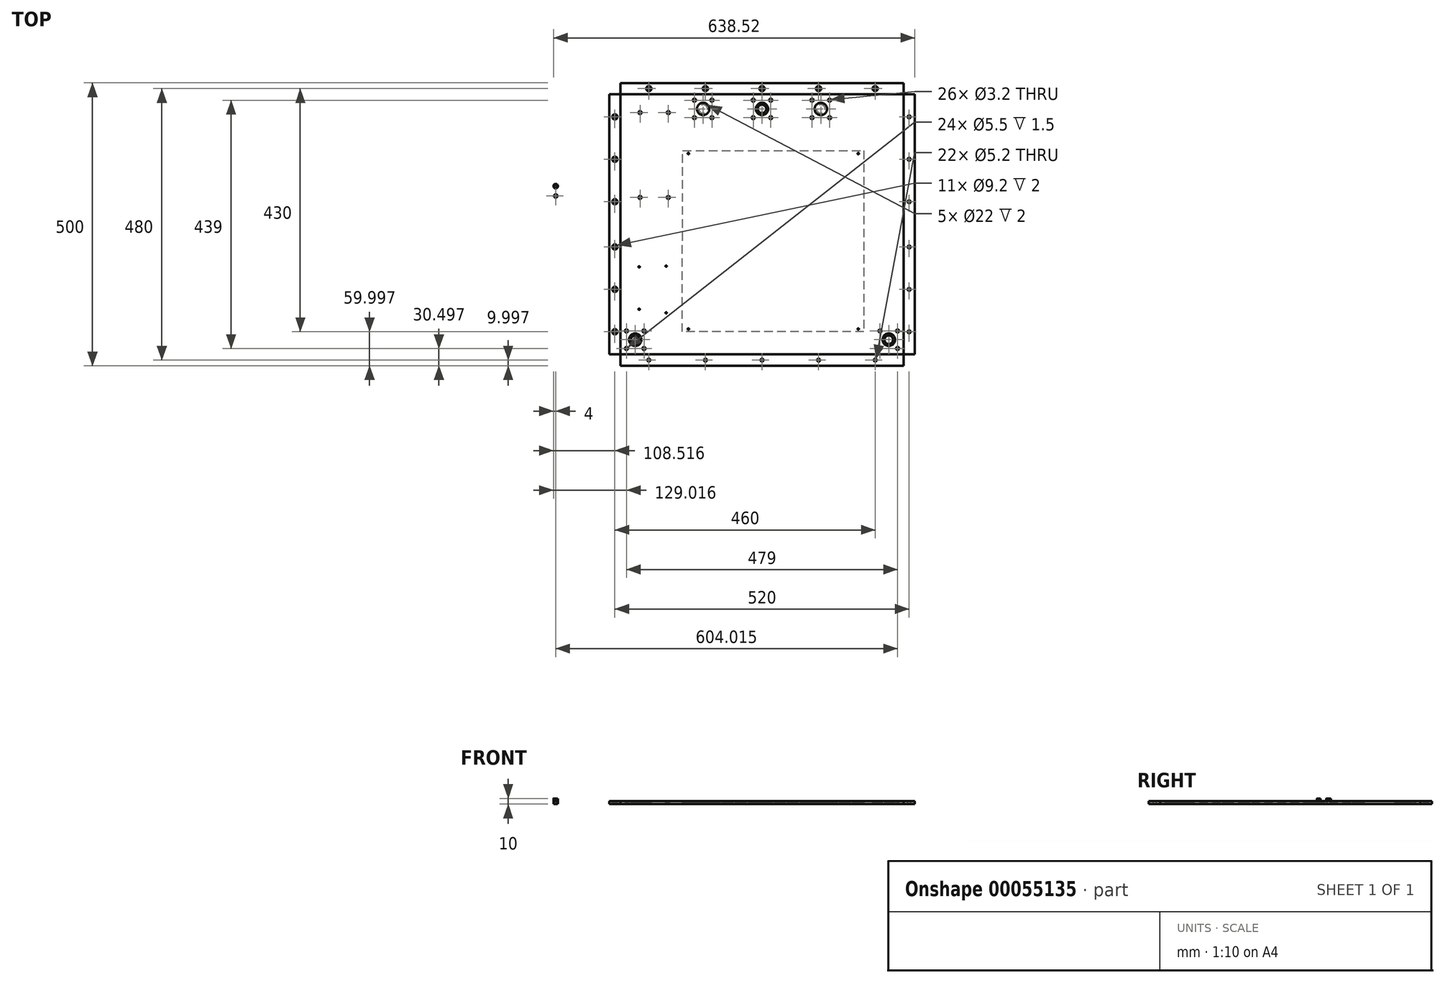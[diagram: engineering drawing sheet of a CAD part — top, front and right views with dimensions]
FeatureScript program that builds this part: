
annotation { "Feature Type Name" : "Feature", "Feature Type Description" : "" }
export const myFeature = defineFeature(function(context is Context, id is Id, definition is map)
    precondition{}
    {
        {
            var Q0;
            Q0=qCreatedBy(makeId("Top.planeOp"),FACE);
            var sketch = newSketch(context, id + "F0", { "sketchPlane" : qUnion([Q0])});
            skLineSegment(sketch, "E0.bottom", {"start": v(-237.36, 309.29) * mm, "end": v(262.64, 309.29) * mm, "construction": true});
            skLineSegment(sketch, "E0.top", {"start": v(-237.36, -150.71) * mm, "end": v(262.64, -150.71) * mm, "construction": true});
            skLineSegment(sketch, "E0.left", {"start": v(-237.36, 309.29) * mm, "end": v(-237.36, -150.71) * mm, "construction": true});
            skLineSegment(sketch, "E0.right", {"start": v(262.64, 309.29) * mm, "end": v(262.64, -150.71) * mm, "construction": true});
            skLineSegment(sketch, "E1.0", {"start": v(-118.36, 309.29) * mm, "end": v(-118.36, -150.71) * mm, "construction": true});
            skLineSegment(sketch, "E2.0", {"start": v(-237.36, 94.29) * mm, "end": v(-117.36, 94.29) * mm, "construction": true});
            skLineSegment(sketch, "E3.0", {"start": v(-202.86, 309.29) * mm, "end": v(-202.86, 94.29) * mm, "construction": true});
            skLineSegment(sketch, "E4.0", {"start": v(-152.86, 309.29) * mm, "end": v(-152.86, 94.29) * mm, "construction": true});
            skLineSegment(sketch, "E5.0", {"start": v(-201.3, 276.79) * mm, "end": v(-118.36, 276.79) * mm, "construction": true});
            skLineSegment(sketch, "E6.0", {"start": v(-201.3, 126.79) * mm, "end": v(-118.36, 126.79) * mm, "construction": true});
            skCircle(sketch, "E7", {"center": v(-202.86, 276.79) * mm, "radius": 1.6 * mm});
            skCircle(sketch, "E8", {"center": v(-152.86, 276.79) * mm, "radius": 1.6 * mm});
            skCircle(sketch, "E9", {"center": v(-152.86, 126.79) * mm, "radius": 1.6 * mm});
            skCircle(sketch, "E10", {"center": v(-202.86, 126.79) * mm, "radius": 1.6 * mm});
            skLineSegment(sketch, "E11.0", {"start": v(182.64, 309.29) * mm, "end": v(182.64, -150.71) * mm, "construction": true});
            skLineSegment(sketch, "E12.0", {"start": v(-117.36, 309.29) * mm, "end": v(-117.36, -150.71) * mm, "construction": true});
            skLineSegment(sketch, "E13.0", {"start": v(197.64, 309.29) * mm, "end": v(197.64, -150.71) * mm, "construction": true});
            skLineSegment(sketch, "E14.0", {"start": v(-132.36, 309.29) * mm, "end": v(-132.36, -150.71) * mm, "construction": true});
            skLineSegment(sketch, "E15.0", {"start": v(-237.36, -140.21) * mm, "end": v(262.64, -140.21) * mm, "construction": true});
            skLineSegment(sketch, "E16.0", {"start": v(-237.36, 298.79) * mm, "end": v(262.64, 298.79) * mm, "construction": true});
            skLineSegment(sketch, "E17.0", {"start": v(-237.36, -109.21) * mm, "end": v(262.64, -109.21) * mm, "construction": true});
            skLineSegment(sketch, "E18.trimOffspring", {"start": v(-226.86, -109.21) * mm, "end": v(-226.86, -140.21) * mm, "construction": true});
            skLineSegment(sketch, "E19.trimOffspring", {"start": v(-195.86, -109.21) * mm, "end": v(-195.86, -140.21) * mm, "construction": true});
            skLineSegment(sketch, "E20", {"start": v(-226.86, -124.71) * mm, "end": v(-195.86, -124.71) * mm, "construction": true});
            skCircle(sketch, "E21", {"center": v(-226.86, -109.21) * mm, "radius": 1.6 * mm});
            skCircle(sketch, "E22", {"center": v(-195.86, -109.21) * mm, "radius": 1.6 * mm});
            skCircle(sketch, "E23", {"center": v(-195.86, -140.21) * mm, "radius": 1.6 * mm});
            skCircle(sketch, "E24", {"center": v(-226.86, -140.21) * mm, "radius": 1.6 * mm});
            skLineSegment(sketch, "E25.trimOffspring", {"start": v(252.14, -109.21) * mm, "end": v(252.14, -140.21) * mm, "construction": true});
            skLineSegment(sketch, "E26.trimOffspring", {"start": v(221.14, -109.21) * mm, "end": v(221.14, -140.21) * mm, "construction": true});
            skLineSegment(sketch, "E27", {"start": v(221.14, -124.71) * mm, "end": v(252.14, -124.71) * mm, "construction": true});
            skCircle(sketch, "E28", {"center": v(221.14, -109.21) * mm, "radius": 1.6 * mm});
            skCircle(sketch, "E29", {"center": v(252.14, -109.21) * mm, "radius": 1.6 * mm});
            skCircle(sketch, "E30", {"center": v(221.14, -140.21) * mm, "radius": 1.6 * mm});
            skCircle(sketch, "E31", {"center": v(252.14, -140.21) * mm, "radius": 1.6 * mm});
            skLineSegment(sketch, "E32.0", {"start": v(-106.86, 309.29) * mm, "end": v(-106.86, 199.29) * mm, "construction": true});
            skLineSegment(sketch, "E33.trimOffspring", {"start": v(197.64, -100.71) * mm, "end": v(262.64, -100.71) * mm, "construction": true});
            skLineSegment(sketch, "E34.trimOffspring", {"start": v(-118.36, 199.29) * mm, "end": v(182.64, 199.29) * mm, "construction": true});
            skLineSegment(sketch, "E35.trimOffspring", {"start": v(-118.36, -100.71) * mm, "end": v(182.64, -100.71) * mm, "construction": true});
            skLineSegment(sketch, "E36.0", {"start": v(132.14, 199.29) * mm, "end": v(132.14, 309.29) * mm, "construction": true});
            skLineSegment(sketch, "E37.0", {"start": v(-75.86, 298.79) * mm, "end": v(-75.86, 267.79) * mm, "construction": true});
            skLineSegment(sketch, "E38.0", {"start": v(101.14, 267.79) * mm, "end": v(101.14, 298.79) * mm, "construction": true});
            skLineSegment(sketch, "E39.0", {"start": v(-237.36, 267.79) * mm, "end": v(262.64, 267.79) * mm, "construction": true});
            skLineSegment(sketch, "E40", {"start": v(101.14, 283.29) * mm, "end": v(132.14, 283.29) * mm, "construction": true});
            skLineSegment(sketch, "E41", {"start": v(-75.86, 283.29) * mm, "end": v(-106.86, 283.29) * mm, "construction": true});
            skCircle(sketch, "E42", {"center": v(101.14, 298.79) * mm, "radius": 1.6 * mm});
            skCircle(sketch, "E43", {"center": v(101.14, 267.79) * mm, "radius": 1.6 * mm});
            skCircle(sketch, "E44", {"center": v(132.14, 298.79) * mm, "radius": 1.6 * mm});
            skCircle(sketch, "E45", {"center": v(132.14, 267.79) * mm, "radius": 1.6 * mm});
            skCircle(sketch, "E46", {"center": v(-75.86, 267.79) * mm, "radius": 1.6 * mm});
            skCircle(sketch, "E47", {"center": v(-75.86, 298.79) * mm, "radius": 1.6 * mm});
            skCircle(sketch, "E48", {"center": v(-106.86, 298.79) * mm, "radius": 1.6 * mm});
            skCircle(sketch, "E49", {"center": v(-106.86, 267.79) * mm, "radius": 1.6 * mm});
            skCircle(sketch, "E50", {"center": v(116.64, 283.29) * mm, "radius": 7.5 * mm});
            skCircle(sketch, "E51", {"center": v(-91.36, 283.29) * mm, "radius": 7.5 * mm});
            skLineSegment(sketch, "E52.0", {"start": v(-237.36, 329.29) * mm, "end": v(262.64, 329.29) * mm});
            skLineSegment(sketch, "E53.0", {"start": v(282.64, 309.29) * mm, "end": v(282.64, -150.71) * mm});
            skLineSegment(sketch, "E54.0", {"start": v(-257.36, 309.29) * mm, "end": v(-257.36, -150.71) * mm});
            skLineSegment(sketch, "E55.0", {"start": v(-237.36, -170.71) * mm, "end": v(262.64, -170.71) * mm});
            skLineSegment(sketch, "E56.0", {"start": v(-237.36, 19.29) * mm, "end": v(-117.36, 19.29) * mm, "construction": true});
            skLineSegment(sketch, "E57.0", {"start": v(-237.36, -84.57) * mm, "end": v(-117.36, -84.57) * mm, "construction": true});
            skLineSegment(sketch, "E58.trimOffspring", {"start": v(-207.36, 19.29) * mm, "end": v(-207.36, -84.57) * mm, "construction": true});
            skLineSegment(sketch, "E59.trimOffspring", {"start": v(-204.36, 19.29) * mm, "end": v(-204.36, -84.57) * mm, "construction": true});
            skLineSegment(sketch, "E60.trimOffspring", {"start": v(-156.66, 19.29) * mm, "end": v(-156.66, -84.57) * mm, "construction": true});
            skLineSegment(sketch, "E61.trimOffspring", {"start": v(-146.14, 19.29) * mm, "end": v(-146.14, -84.57) * mm, "construction": true});
            skLineSegment(sketch, "E62.0", {"start": v(-207.36, 5.39) * mm, "end": v(-146.14, 5.39) * mm, "construction": true});
            skLineSegment(sketch, "E63.0", {"start": v(-207.36, 4.14) * mm, "end": v(-146.14, 4.14) * mm, "construction": true});
            skLineSegment(sketch, "E64.0", {"start": v(-207.36, -70.81) * mm, "end": v(-146.14, -70.81) * mm, "construction": true});
            skLineSegment(sketch, "E65.0", {"start": v(-207.36, -77.16) * mm, "end": v(-146.14, -77.16) * mm, "construction": true});
            skCircle(sketch, "E66", {"center": v(-204.36, 4.14) * mm, "radius": 1.25 * mm});
            skCircle(sketch, "E67", {"center": v(-156.66, 5.39) * mm, "radius": 1.25 * mm});
            skCircle(sketch, "E68", {"center": v(-156.66, -77.16) * mm, "radius": 1.25 * mm});
            skCircle(sketch, "E69", {"center": v(-204.36, -70.81) * mm, "radius": 1.25 * mm});
            skLineSegment(sketch, "E70", {"start": v(262.64, 329.29) * mm, "end": v(262.64, 309.29) * mm});
            skLineSegment(sketch, "E71", {"start": v(262.64, 309.29) * mm, "end": v(282.64, 309.29) * mm});
            skLineSegment(sketch, "E72", {"start": v(-237.36, 329.29) * mm, "end": v(-237.36, 309.29) * mm});
            skLineSegment(sketch, "E73", {"start": v(-257.36, 309.29) * mm, "end": v(-237.36, 309.29) * mm});
            skLineSegment(sketch, "E74", {"start": v(-257.36, -150.71) * mm, "end": v(-237.36, -150.71) * mm});
            skLineSegment(sketch, "E75", {"start": v(-237.36, -170.71) * mm, "end": v(-237.36, -150.71) * mm});
            skLineSegment(sketch, "E76", {"start": v(262.64, -170.71) * mm, "end": v(262.64, -150.71) * mm});
            skLineSegment(sketch, "E77", {"start": v(282.64, -150.71) * mm, "end": v(262.64, -150.71) * mm});
            skLineSegment(sketch, "E78.0", {"start": v(-237.36, 319.29) * mm, "end": v(262.64, 319.29) * mm, "construction": true});
            skLineSegment(sketch, "E79.0", {"start": v(-247.36, 309.29) * mm, "end": v(-247.36, -150.71) * mm, "construction": true});
            skLineSegment(sketch, "E80.0", {"start": v(-257.36, -110.71) * mm, "end": v(-237.36, -110.71) * mm, "construction": true});
            skLineSegment(sketch, "E81.0", {"start": v(-257.36, -35.71) * mm, "end": v(-237.36, -35.71) * mm, "construction": true});
            skLineSegment(sketch, "E82.0", {"start": v(-257.36, 39.29) * mm, "end": v(-237.36, 39.29) * mm, "construction": true});
            skLineSegment(sketch, "E83.0", {"start": v(-257.36, 119.29) * mm, "end": v(-237.36, 119.29) * mm, "construction": true});
            skLineSegment(sketch, "E84.0", {"start": v(-257.36, 194.29) * mm, "end": v(-237.36, 194.29) * mm, "construction": true});
            skLineSegment(sketch, "E85.0", {"start": v(-257.36, 269.29) * mm, "end": v(-237.36, 269.29) * mm, "construction": true});
            skCircle(sketch, "E86", {"center": v(-247.36, 39.29) * mm, "radius": 2.6 * mm});
            skCircle(sketch, "E87", {"center": v(-247.36, 119.29) * mm, "radius": 2.6 * mm});
            skCircle(sketch, "E88", {"center": v(-247.36, 194.29) * mm, "radius": 2.6 * mm});
            skCircle(sketch, "E89", {"center": v(-247.36, 269.29) * mm, "radius": 2.6 * mm});
            skCircle(sketch, "E90", {"center": v(-247.36, -35.71) * mm, "radius": 2.6 * mm});
            skCircle(sketch, "E91", {"center": v(-247.36, -110.71) * mm, "radius": 2.6 * mm});
            skLineSegment(sketch, "E92", {"start": v(12.64, 329.29) * mm, "end": v(12.64, 425.64) * mm});
            skCircle(sketch, "E93.MirrorC", {"center": v(272.64, -110.71) * mm, "radius": 2.6 * mm});
            skCircle(sketch, "E94.MirrorC", {"center": v(272.64, -35.71) * mm, "radius": 2.6 * mm});
            skCircle(sketch, "E95.MirrorC", {"center": v(272.64, 39.29) * mm, "radius": 2.6 * mm});
            skCircle(sketch, "E96.MirrorC", {"center": v(272.64, 119.29) * mm, "radius": 2.6 * mm});
            skCircle(sketch, "E97.MirrorC", {"center": v(272.64, 194.29) * mm, "radius": 2.6 * mm});
            skCircle(sketch, "E98.MirrorC", {"center": v(272.64, 269.29) * mm, "radius": 2.6 * mm});
            skLineSegment(sketch, "E99.0", {"start": v(-187.36, 329.29) * mm, "end": v(-187.36, 309.29) * mm, "construction": true});
            skLineSegment(sketch, "E100.0", {"start": v(-87.36, 329.29) * mm, "end": v(-87.36, 309.29) * mm, "construction": true});
            skLineSegment(sketch, "E101.0", {"start": v(212.64, 329.29) * mm, "end": v(212.64, 309.29) * mm, "construction": true});
            skLineSegment(sketch, "E102.0", {"start": v(112.64, 329.29) * mm, "end": v(112.64, 309.29) * mm, "construction": true});
            skCircle(sketch, "E103", {"center": v(-187.36, 319.29) * mm, "radius": 2.6 * mm});
            skCircle(sketch, "E104", {"center": v(-87.36, 319.29) * mm, "radius": 2.6 * mm});
            skCircle(sketch, "E105", {"center": v(12.64, 319.29) * mm, "radius": 2.6 * mm});
            skCircle(sketch, "E106", {"center": v(112.64, 319.29) * mm, "radius": 2.6 * mm});
            skCircle(sketch, "E107", {"center": v(212.64, 319.29) * mm, "radius": 2.6 * mm});
            skLineSegment(sketch, "E108", {"start": v(282.64, 79.29) * mm, "end": v(335.67, 79.29) * mm});
            skCircle(sketch, "E109.MirrorC", {"center": v(212.64, -160.71) * mm, "radius": 2.6 * mm});
            skCircle(sketch, "E110.MirrorC", {"center": v(112.64, -160.71) * mm, "radius": 2.6 * mm});
            skCircle(sketch, "E111.MirrorC", {"center": v(12.64, -160.71) * mm, "radius": 2.6 * mm});
            skCircle(sketch, "E112.MirrorC", {"center": v(-87.36, -160.71) * mm, "radius": 2.6 * mm});
            skCircle(sketch, "E113.MirrorC", {"center": v(-187.36, -160.71) * mm, "radius": 2.6 * mm});
            skCircle(sketch, "E114", {"center": v(-211.36, -124.71) * mm, "radius": 7.5 * mm});
            skCircle(sketch, "E115", {"center": v(236.64, -124.71) * mm, "radius": 7.5 * mm});
            skLineSegment(sketch, "E116", {"start": v(12.64, 267.79) * mm, "end": v(12.64, 298.79) * mm, "construction": true});
            skLineSegment(sketch, "E117.0", {"start": v(28.14, 267.79) * mm, "end": v(28.14, 298.79) * mm, "construction": true});
            skLineSegment(sketch, "E118.0", {"start": v(-2.86, 267.79) * mm, "end": v(-2.86, 298.79) * mm, "construction": true});
            skCircle(sketch, "E119", {"center": v(12.64, 283.29) * mm, "radius": 7.5 * mm});
            skCircle(sketch, "E120", {"center": v(-2.86, 298.79) * mm, "radius": 1.6 * mm});
            skCircle(sketch, "E121", {"center": v(28.14, 298.79) * mm, "radius": 1.6 * mm});
            skCircle(sketch, "E122", {"center": v(28.14, 267.79) * mm, "radius": 1.6 * mm});
            skCircle(sketch, "E123", {"center": v(-2.86, 267.79) * mm, "radius": 1.6 * mm});
            skSolve(sketch);
        }
        {
            var Q0;
            Q0=qCreatedBy(makeId("Top.planeOp"),FACE);
            var sketch = newSketch(context, id + "F1", { "sketchPlane" : qUnion([Q0])});
            skLineSegment(sketch, "E124.bottom", {"start": v(-558.04, 48.55) * mm, "end": v(-516.04, 48.55) * mm, "construction": true});
            skLineSegment(sketch, "E124.top", {"start": v(-558.04, 1.55) * mm, "end": v(-516.04, 1.55) * mm, "construction": true});
            skLineSegment(sketch, "E124.right", {"start": v(-516.04, 48.55) * mm, "end": v(-516.04, 1.55) * mm, "construction": true});
            skLineSegment(sketch, "E125", {"start": v(-558.04, -28.45) * mm, "end": v(-558.04, 1.55) * mm});
            skLineSegment(sketch, "E126.1", {"start": v(-515.04, 48.55) * mm, "end": v(-515.04, 1.55) * mm, "construction": true});
            skLineSegment(sketch, "E127.0", {"start": v(-473.04, -28.45) * mm, "end": v(-473.04, 1.55) * mm});
            skLineSegment(sketch, "E127.1", {"start": v(-473.04, 48.55) * mm, "end": v(-473.04, 1.55) * mm});
            skLineSegment(sketch, "E128", {"start": v(-515.04, 48.55) * mm, "end": v(-473.04, 48.55) * mm, "construction": true});
            skLineSegment(sketch, "E129", {"start": v(-515.04, 1.55) * mm, "end": v(-473.04, 1.55) * mm, "construction": true});
            skLineSegment(sketch, "E130.bottom", {"start": v(-473.04, -28.45) * mm, "end": v(-558.04, -28.45) * mm});
            skLineSegment(sketch, "E130.top", {"start": v(-473.04, 53.55) * mm, "end": v(-558.04, 53.55) * mm});
            skLineSegment(sketch, "E130.left", {"start": v(-473.04, -28.45) * mm, "end": v(-473.04, 53.55) * mm});
            skLineSegment(sketch, "E131", {"start": v(-558.04, -13.45) * mm, "end": v(-516.04, -13.45) * mm, "construction": true});
            skLineSegment(sketch, "E132.0", {"start": v(-473.04, 75.55) * mm, "end": v(-558.04, 75.55) * mm});
            skLineSegment(sketch, "E133", {"start": v(-558.04, 1.55) * mm, "end": v(-558.04, 53.55) * mm});
            skLineSegment(sketch, "E134", {"start": v(-516.04, 1.55) * mm, "end": v(-516.04, -28.45) * mm, "construction": true});
            skLineSegment(sketch, "E135", {"start": v(-515.04, 1.55) * mm, "end": v(-515.04, -28.45) * mm, "construction": true});
            skLineSegment(sketch, "E136.trimOffspring", {"start": v(-515.04, -13.45) * mm, "end": v(-473.04, -13.45) * mm, "construction": true});
            skCircle(sketch, "E137", {"center": v(-537.04, -13.45) * mm, "radius": 8.5 * mm});
            skCircle(sketch, "E138", {"center": v(-494.04, -13.45) * mm, "radius": 8.5 * mm});
            skSolve(sketch);
        }
        {
            var Q0;
            Q0=makeQuery(id+"F0.imprint","IMPRINT",FACE,{"disambiguationData":[TD([[makeQuery(id+"F0.imprint","IMPRINT",EDGE,{"derivedFrom":sQuery(id+"F0.wireOp",EDGE,"E7")}),-1.0]])]});
            extrude(context, id + "F2", {"entities" : qUnion([Q0]), "depth" : 5 * mm});
        }
        {
            var Q0;
            Q0=makeQuery(id+"F2.opExtrude","CAP_FACE",FACE,{"disambiguationData":[OSD([sQuery(id+"F0.wireOp",EDGE,"E7"),sQuery(id+"F0.wireOp",EDGE,"E8"),sQuery(id+"F0.wireOp",EDGE,"E9"),sQuery(id+"F0.wireOp",EDGE,"E10"),sQuery(id+"F0.wireOp",EDGE,"C0uSwMvh-bZ3V-A5UR-ObhC-SuazAej5d5Y7"),sQuery(id+"F0.wireOp",EDGE,"E21"),sQuery(id+"F0.wireOp",EDGE,"E22"),sQuery(id+"F0.wireOp",EDGE,"E23"),sQuery(id+"F0.wireOp",EDGE,"E24"),sQuery(id+"F0.wireOp",EDGE,"E28"),sQuery(id+"F0.wireOp",EDGE,"E29"),sQuery(id+"F0.wireOp",EDGE,"E30"),sQuery(id+"F0.wireOp",EDGE,"XtzUmerH-F8ZK-TeMd-aJrn-KmrtfTiEuZh9"),sQuery(id+"F0.wireOp",EDGE,"E31"),sQuery(id+"F0.wireOp",EDGE,"ix5QspZB-ting-d7O3-eglK-wTbe0T3LvuQs"),sQuery(id+"F0.wireOp",EDGE,"50q9mh1O-mLyt-XYZc-9GO9-dTGnbKH8VegG"),sQuery(id+"F0.wireOp",EDGE,"E42"),sQuery(id+"F0.wireOp",EDGE,"E43"),sQuery(id+"F0.wireOp",EDGE,"E44"),sQuery(id+"F0.wireOp",EDGE,"E45"),sQuery(id+"F0.wireOp",EDGE,"E46"),sQuery(id+"F0.wireOp",EDGE,"E47"),sQuery(id+"F0.wireOp",EDGE,"E48"),sQuery(id+"F0.wireOp",EDGE,"E49"),sQuery(id+"F0.wireOp",EDGE,"E52.0"),sQuery(id+"F0.wireOp",EDGE,"E53.0"),sQuery(id+"F0.wireOp",EDGE,"E54.0"),sQuery(id+"F0.wireOp",EDGE,"E55.0"),sQuery(id+"F0.wireOp",EDGE,"E66"),sQuery(id+"F0.wireOp",EDGE,"E67"),sQuery(id+"F0.wireOp",EDGE,"E68"),sQuery(id+"F0.wireOp",EDGE,"E69"),sQuery(id+"F0.wireOp",EDGE,"E70"),sQuery(id+"F0.wireOp",EDGE,"E71"),sQuery(id+"F0.wireOp",EDGE,"E72"),sQuery(id+"F0.wireOp",EDGE,"E73"),sQuery(id+"F0.wireOp",EDGE,"E74"),sQuery(id+"F0.wireOp",EDGE,"E75"),sQuery(id+"F0.wireOp",EDGE,"E76"),sQuery(id+"F0.wireOp",EDGE,"E77"),sQuery(id+"F0.wireOp",EDGE,"E86"),sQuery(id+"F0.wireOp",EDGE,"E87"),sQuery(id+"F0.wireOp",EDGE,"E88"),sQuery(id+"F0.wireOp",EDGE,"E89"),sQuery(id+"F0.wireOp",EDGE,"E90"),sQuery(id+"F0.wireOp",EDGE,"E91"),sQuery(id+"F0.wireOp",EDGE,"E93.MirrorC"),sQuery(id+"F0.wireOp",EDGE,"E94.MirrorC"),sQuery(id+"F0.wireOp",EDGE,"E95.MirrorC"),sQuery(id+"F0.wireOp",EDGE,"E96.MirrorC"),sQuery(id+"F0.wireOp",EDGE,"E97.MirrorC"),sQuery(id+"F0.wireOp",EDGE,"E98.MirrorC"),sQuery(id+"F0.wireOp",EDGE,"E103"),sQuery(id+"F0.wireOp",EDGE,"E104"),sQuery(id+"F0.wireOp",EDGE,"E105"),sQuery(id+"F0.wireOp",EDGE,"E106"),sQuery(id+"F0.wireOp",EDGE,"E107"),sQuery(id+"F0.wireOp",EDGE,"E109.MirrorC"),sQuery(id+"F0.wireOp",EDGE,"E110.MirrorC"),sQuery(id+"F0.wireOp",EDGE,"E111.MirrorC"),sQuery(id+"F0.wireOp",EDGE,"E112.MirrorC"),sQuery(id+"F0.wireOp",EDGE,"E113.MirrorC")])],"isStart":false});
            var sketch = newSketch(context, id + "F3", { "sketchPlane" : qUnion([Q0])});
            skCircle(sketch, "E139.0", {"center": v(-202.86, 276.79) * mm, "radius": 1.6 * mm});
            skCircle(sketch, "E139.1", {"center": v(-152.86, 276.79) * mm, "radius": 1.6 * mm});
            skCircle(sketch, "E139.2", {"center": v(-106.86, 267.79) * mm, "radius": 1.6 * mm});
            skCircle(sketch, "E139.3", {"center": v(-106.86, 298.79) * mm, "radius": 1.6 * mm});
            skCircle(sketch, "E139.4", {"center": v(-75.86, 267.79) * mm, "radius": 1.6 * mm});
            skCircle(sketch, "E139.5", {"center": v(-75.86, 298.79) * mm, "radius": 1.6 * mm});
            skCircle(sketch, "E139.7", {"center": v(132.14, 267.79) * mm, "radius": 1.6 * mm});
            skCircle(sketch, "E139.8", {"center": v(132.14, 298.79) * mm, "radius": 1.6 * mm});
            skCircle(sketch, "E139.9", {"center": v(101.14, 298.79) * mm, "radius": 1.6 * mm});
            skCircle(sketch, "E139.10", {"center": v(101.14, 267.79) * mm, "radius": 1.6 * mm});
            skCircle(sketch, "E139.11", {"center": v(-202.86, 126.79) * mm, "radius": 1.6 * mm});
            skCircle(sketch, "E139.12", {"center": v(-152.86, 126.79) * mm, "radius": 1.6 * mm});
            skCircle(sketch, "E139.13", {"center": v(-204.36, 4.14) * mm, "radius": 1.25 * mm});
            skCircle(sketch, "E139.14", {"center": v(-156.66, 5.39) * mm, "radius": 1.25 * mm});
            skCircle(sketch, "E139.15", {"center": v(-156.66, -77.16) * mm, "radius": 1.25 * mm});
            skCircle(sketch, "E139.16", {"center": v(-204.36, -70.81) * mm, "radius": 1.25 * mm});
            skCircle(sketch, "E139.17", {"center": v(-195.86, -109.21) * mm, "radius": 1.6 * mm});
            skCircle(sketch, "E139.18", {"center": v(-226.86, -109.21) * mm, "radius": 1.6 * mm});
            skCircle(sketch, "E139.19", {"center": v(-226.86, -140.21) * mm, "radius": 1.6 * mm});
            skCircle(sketch, "E139.20", {"center": v(-195.86, -140.21) * mm, "radius": 1.6 * mm});
            skCircle(sketch, "E139.23", {"center": v(252.14, -140.21) * mm, "radius": 1.6 * mm});
            skCircle(sketch, "E139.24", {"center": v(252.14, -109.21) * mm, "radius": 1.6 * mm});
            skCircle(sketch, "E139.25", {"center": v(221.14, -109.21) * mm, "radius": 1.6 * mm});
            skCircle(sketch, "E139.26", {"center": v(221.14, -140.21) * mm, "radius": 1.6 * mm});
            skCircle(sketch, "E139.27", {"center": v(272.64, -110.71) * mm, "radius": 2.6 * mm});
            skCircle(sketch, "E139.28", {"center": v(212.64, -160.71) * mm, "radius": 2.6 * mm});
            skCircle(sketch, "E139.29", {"center": v(272.64, -35.71) * mm, "radius": 2.6 * mm});
            skCircle(sketch, "E139.30", {"center": v(112.64, -160.71) * mm, "radius": 2.6 * mm});
            skCircle(sketch, "E139.31", {"center": v(272.64, 39.29) * mm, "radius": 2.6 * mm});
            skCircle(sketch, "E139.32", {"center": v(272.64, 119.29) * mm, "radius": 2.6 * mm});
            skCircle(sketch, "E139.33", {"center": v(272.64, 194.29) * mm, "radius": 2.6 * mm});
            skCircle(sketch, "E139.34", {"center": v(272.64, 269.29) * mm, "radius": 2.6 * mm});
            skCircle(sketch, "E139.35", {"center": v(212.64, 319.29) * mm, "radius": 2.6 * mm});
            skCircle(sketch, "E139.36", {"center": v(112.64, 319.29) * mm, "radius": 2.6 * mm});
            skCircle(sketch, "E139.37", {"center": v(12.64, 319.29) * mm, "radius": 2.6 * mm});
            skCircle(sketch, "E139.38", {"center": v(-87.36, 319.29) * mm, "radius": 2.6 * mm});
            skCircle(sketch, "E139.39", {"center": v(-187.36, 319.29) * mm, "radius": 2.6 * mm});
            skCircle(sketch, "E139.40", {"center": v(-247.36, 269.29) * mm, "radius": 2.6 * mm});
            skCircle(sketch, "E139.41", {"center": v(-247.36, 194.29) * mm, "radius": 2.6 * mm});
            skCircle(sketch, "E139.42", {"center": v(-247.36, 119.29) * mm, "radius": 2.6 * mm});
            skCircle(sketch, "E139.43", {"center": v(-247.36, 39.29) * mm, "radius": 2.6 * mm});
            skCircle(sketch, "E139.44", {"center": v(-247.36, -35.71) * mm, "radius": 2.6 * mm});
            skCircle(sketch, "E139.45", {"center": v(-247.36, -110.71) * mm, "radius": 2.6 * mm});
            skCircle(sketch, "E139.46", {"center": v(-187.36, -160.71) * mm, "radius": 2.6 * mm});
            skCircle(sketch, "E139.47", {"center": v(-87.36, -160.71) * mm, "radius": 2.6 * mm});
            skCircle(sketch, "E139.48", {"center": v(12.64, -160.71) * mm, "radius": 2.6 * mm});
            skCircle(sketch, "E140.0", {"center": v(-91.36, 283.29) * mm, "radius": 7.5 * mm});
            skCircle(sketch, "E140.1", {"center": v(116.64, 283.29) * mm, "radius": 7.5 * mm});
            skCircle(sketch, "E140.2", {"center": v(236.64, -124.71) * mm, "radius": 7.5 * mm});
            skCircle(sketch, "E140.3", {"center": v(-211.36, -124.71) * mm, "radius": 7.5 * mm});
            skCircle(sketch, "E141.0", {"center": v(-211.36, -124.71) * mm, "radius": 11 * mm});
            skCircle(sketch, "E142.0", {"center": v(236.64, -124.71) * mm, "radius": 11 * mm});
            skCircle(sketch, "E143.0", {"center": v(116.64, 283.29) * mm, "radius": 11 * mm});
            skCircle(sketch, "E144.0", {"center": v(-91.36, 283.29) * mm, "radius": 11 * mm});
            skCircle(sketch, "E145.0", {"center": v(-247.36, 269.29) * mm, "radius": 4.6 * mm});
            skCircle(sketch, "E146", {"center": v(-187.36, 319.29) * mm, "radius": 4.6 * mm});
            skCircle(sketch, "E147", {"center": v(-202.86, 276.79) * mm, "radius": 2.75 * mm});
            skCircle(sketch, "E148", {"center": v(-152.86, 276.79) * mm, "radius": 2.75 * mm});
            skCircle(sketch, "E149", {"center": v(-106.86, 267.79) * mm, "radius": 2.75 * mm});
            skCircle(sketch, "E150", {"center": v(-87.36, 319.29) * mm, "radius": 4.6 * mm});
            skCircle(sketch, "E151", {"center": v(12.64, 319.29) * mm, "radius": 4.6 * mm});
            skCircle(sketch, "E152", {"center": v(112.64, 319.29) * mm, "radius": 4.6 * mm});
            skCircle(sketch, "E153", {"center": v(212.64, 319.29) * mm, "radius": 4.6 * mm});
            skCircle(sketch, "E154", {"center": v(272.64, 269.29) * mm, "radius": 4.6 * mm});
            skCircle(sketch, "E155", {"center": v(-106.86, 298.79) * mm, "radius": 2.75 * mm});
            skCircle(sketch, "E156", {"center": v(-75.86, 298.79) * mm, "radius": 2.75 * mm});
            skCircle(sketch, "E157", {"center": v(-75.86, 267.79) * mm, "radius": 2.75 * mm});
            skCircle(sketch, "E158", {"center": v(101.14, 298.79) * mm, "radius": 2.75 * mm});
            skCircle(sketch, "E159", {"center": v(101.14, 267.79) * mm, "radius": 2.75 * mm});
            skCircle(sketch, "E160", {"center": v(132.14, 298.79) * mm, "radius": 2.75 * mm});
            skCircle(sketch, "E161", {"center": v(-247.36, 194.29) * mm, "radius": 4.6 * mm});
            skCircle(sketch, "E162", {"center": v(-247.36, 119.29) * mm, "radius": 4.6 * mm});
            skCircle(sketch, "E163", {"center": v(-202.86, 126.79) * mm, "radius": 2.75 * mm});
            skCircle(sketch, "E164", {"center": v(-152.86, 126.79) * mm, "radius": 2.75 * mm});
            skCircle(sketch, "E165", {"center": v(-247.36, 39.29) * mm, "radius": 4.6 * mm});
            skCircle(sketch, "E166", {"center": v(-247.36, -35.71) * mm, "radius": 4.6 * mm});
            skCircle(sketch, "E167", {"center": v(-247.36, -110.71) * mm, "radius": 4.6 * mm});
            skCircle(sketch, "E168", {"center": v(-187.36, -160.71) * mm, "radius": 4.6 * mm});
            skCircle(sketch, "E169", {"center": v(-87.36, -160.71) * mm, "radius": 4.6 * mm});
            skCircle(sketch, "E170", {"center": v(12.64, -160.71) * mm, "radius": 4.6 * mm});
            skCircle(sketch, "E171", {"center": v(112.64, -160.71) * mm, "radius": 4.6 * mm});
            skCircle(sketch, "E172", {"center": v(-195.86, -109.21) * mm, "radius": 2.75 * mm});
            skCircle(sketch, "E173", {"center": v(-226.86, -109.21) * mm, "radius": 2.75 * mm});
            skCircle(sketch, "E174", {"center": v(-226.86, -140.21) * mm, "radius": 2.75 * mm});
            skCircle(sketch, "E175", {"center": v(-195.86, -140.21) * mm, "radius": 2.75 * mm});
            skCircle(sketch, "E176", {"center": v(272.64, 39.29) * mm, "radius": 4.6 * mm});
            skCircle(sketch, "E177", {"center": v(272.64, -35.71) * mm, "radius": 4.6 * mm});
            skCircle(sketch, "E178", {"center": v(272.64, -110.71) * mm, "radius": 4.6 * mm});
            skCircle(sketch, "E179", {"center": v(221.14, -109.21) * mm, "radius": 2.75 * mm});
            skCircle(sketch, "E180", {"center": v(252.14, -140.21) * mm, "radius": 2.75 * mm});
            skCircle(sketch, "E181", {"center": v(221.14, -140.21) * mm, "radius": 2.75 * mm});
            skCircle(sketch, "E182", {"center": v(252.14, -109.21) * mm, "radius": 2.75 * mm});
            skCircle(sketch, "E183", {"center": v(272.64, 119.29) * mm, "radius": 4.6 * mm});
            skCircle(sketch, "E184", {"center": v(272.64, 194.29) * mm, "radius": 4.6 * mm});
            skCircle(sketch, "E185", {"center": v(132.14, 267.79) * mm, "radius": 2.75 * mm});
            skCircle(sketch, "E186", {"center": v(212.64, -160.71) * mm, "radius": 4.6 * mm});
            skCircle(sketch, "E187.0", {"center": v(12.64, 283.29) * mm, "radius": 7.5 * mm});
            skCircle(sketch, "E187.1", {"center": v(-2.86, 298.79) * mm, "radius": 1.6 * mm});
            skCircle(sketch, "E187.2", {"center": v(28.14, 298.79) * mm, "radius": 1.6 * mm});
            skCircle(sketch, "E187.3", {"center": v(28.14, 267.79) * mm, "radius": 1.6 * mm});
            skCircle(sketch, "E187.4", {"center": v(-2.86, 267.79) * mm, "radius": 1.6 * mm});
            skCircle(sketch, "E188.0", {"center": v(12.64, 283.29) * mm, "radius": 11 * mm});
            skCircle(sketch, "E189", {"center": v(-2.86, 298.79) * mm, "radius": 2.75 * mm});
            skCircle(sketch, "E190", {"center": v(28.14, 298.79) * mm, "radius": 2.75 * mm});
            skCircle(sketch, "E191", {"center": v(28.14, 267.79) * mm, "radius": 2.75 * mm});
            skCircle(sketch, "E192", {"center": v(-2.86, 267.79) * mm, "radius": 2.75 * mm});
            skSolve(sketch);
        }
        {
            var Q0;
            Q0=makeQuery(id+"F3.imprint","IMPRINT",FACE,{"disambiguationData":[TD([[makeQuery(id+"F3.imprint","IMPRINT",EDGE,{"derivedFrom":sQuery(id+"F3.wireOp",EDGE,"E139.3")}),-1.0]])]});
            var Q1;
            Q1=makeQuery(id+"F3.imprint","IMPRINT",FACE,{"disambiguationData":[TD([[makeQuery(id+"F3.imprint","IMPRINT",EDGE,{"derivedFrom":sQuery(id+"F3.wireOp",EDGE,"E139.5")}),-1.0]])]});
            var Q2;
            Q2=makeQuery(id+"F3.imprint","IMPRINT",FACE,{"disambiguationData":[TD([[makeQuery(id+"F3.imprint","IMPRINT",EDGE,{"derivedFrom":sQuery(id+"F3.wireOp",EDGE,"E139.4")}),-1.0]])]});
            var Q3;
            Q3=makeQuery(id+"F3.imprint","IMPRINT",FACE,{"disambiguationData":[TD([[makeQuery(id+"F3.imprint","IMPRINT",EDGE,{"derivedFrom":sQuery(id+"F3.wireOp",EDGE,"E139.2")}),-1.0]])]});
            var Q4;
            Q4=makeQuery(id+"F3.imprint","IMPRINT",FACE,{"disambiguationData":[TD([[makeQuery(id+"F3.imprint","IMPRINT",EDGE,{"derivedFrom":sQuery(id+"F3.wireOp",EDGE,"E139.0")}),-1.0]])]});
            var Q5;
            Q5=makeQuery(id+"F3.imprint","IMPRINT",FACE,{"disambiguationData":[TD([[makeQuery(id+"F3.imprint","IMPRINT",EDGE,{"derivedFrom":sQuery(id+"F3.wireOp",EDGE,"E139.1")}),-1.0]])]});
            var Q6;
            Q6=makeQuery(id+"F3.imprint","IMPRINT",FACE,{"disambiguationData":[TD([[makeQuery(id+"F3.imprint","IMPRINT",EDGE,{"derivedFrom":sQuery(id+"F3.wireOp",EDGE,"E139.11")}),-1.0]])]});
            var Q7;
            Q7=makeQuery(id+"F3.imprint","IMPRINT",FACE,{"disambiguationData":[TD([[makeQuery(id+"F3.imprint","IMPRINT",EDGE,{"derivedFrom":sQuery(id+"F3.wireOp",EDGE,"E139.12")}),-1.0]])]});
            var Q8;
            Q8=makeQuery(id+"F3.imprint","IMPRINT",FACE,{"disambiguationData":[TD([[makeQuery(id+"F3.imprint","IMPRINT",EDGE,{"derivedFrom":sQuery(id+"F3.wireOp",EDGE,"E139.18")}),-1.0]])]});
            var Q9;
            Q9=makeQuery(id+"F3.imprint","IMPRINT",FACE,{"disambiguationData":[TD([[makeQuery(id+"F3.imprint","IMPRINT",EDGE,{"derivedFrom":sQuery(id+"F3.wireOp",EDGE,"E139.17")}),-1.0]])]});
            var Q10;
            Q10=makeQuery(id+"F3.imprint","IMPRINT",FACE,{"disambiguationData":[TD([[makeQuery(id+"F3.imprint","IMPRINT",EDGE,{"derivedFrom":sQuery(id+"F3.wireOp",EDGE,"E139.20")}),-1.0]])]});
            var Q11;
            Q11=makeQuery(id+"F3.imprint","IMPRINT",FACE,{"disambiguationData":[TD([[makeQuery(id+"F3.imprint","IMPRINT",EDGE,{"derivedFrom":sQuery(id+"F3.wireOp",EDGE,"E139.19")}),-1.0]])]});
            var Q12;
            Q12=makeQuery(id+"F3.imprint","IMPRINT",FACE,{"disambiguationData":[TD([[makeQuery(id+"F3.imprint","IMPRINT",EDGE,{"derivedFrom":sQuery(id+"F3.wireOp",EDGE,"E139.24")}),-1.0]])]});
            var Q13;
            Q13=makeQuery(id+"F3.imprint","IMPRINT",FACE,{"disambiguationData":[TD([[makeQuery(id+"F3.imprint","IMPRINT",EDGE,{"derivedFrom":sQuery(id+"F3.wireOp",EDGE,"E139.25")}),-1.0]])]});
            var Q14;
            Q14=makeQuery(id+"F3.imprint","IMPRINT",FACE,{"disambiguationData":[TD([[makeQuery(id+"F3.imprint","IMPRINT",EDGE,{"derivedFrom":sQuery(id+"F3.wireOp",EDGE,"E139.26")}),-1.0]])]});
            var Q15;
            Q15=makeQuery(id+"F3.imprint","IMPRINT",FACE,{"disambiguationData":[TD([[makeQuery(id+"F3.imprint","IMPRINT",EDGE,{"derivedFrom":sQuery(id+"F3.wireOp",EDGE,"E139.23")}),-1.0]])]});
            var Q16;
            Q16=makeQuery(id+"F3.imprint","IMPRINT",FACE,{"disambiguationData":[TD([[makeQuery(id+"F3.imprint","IMPRINT",EDGE,{"derivedFrom":sQuery(id+"F3.wireOp",EDGE,"E139.9")}),-1.0]])]});
            var Q17;
            Q17=makeQuery(id+"F3.imprint","IMPRINT",FACE,{"disambiguationData":[TD([[makeQuery(id+"F3.imprint","IMPRINT",EDGE,{"derivedFrom":sQuery(id+"F3.wireOp",EDGE,"E139.10")}),-1.0]])]});
            var Q18;
            Q18=makeQuery(id+"F3.imprint","IMPRINT",FACE,{"disambiguationData":[TD([[makeQuery(id+"F3.imprint","IMPRINT",EDGE,{"derivedFrom":sQuery(id+"F3.wireOp",EDGE,"E139.8")}),-1.0]])]});
            var Q19;
            Q19=makeQuery(id+"F3.imprint","IMPRINT",FACE,{"disambiguationData":[TD([[makeQuery(id+"F3.imprint","IMPRINT",EDGE,{"derivedFrom":sQuery(id+"F3.wireOp",EDGE,"E139.7")}),-1.0]])]});
            var Q20;
            Q20=makeQuery(id+"F3.imprint","IMPRINT",FACE,{"disambiguationData":[TD([[makeQuery(id+"F3.imprint","IMPRINT",EDGE,{"derivedFrom":sQuery(id+"F3.wireOp",EDGE,"E187.1")}),-1.0]])]});
            var Q21;
            Q21=makeQuery(id+"F3.imprint","IMPRINT",FACE,{"disambiguationData":[TD([[makeQuery(id+"F3.imprint","IMPRINT",EDGE,{"derivedFrom":sQuery(id+"F3.wireOp",EDGE,"E187.2")}),-1.0]])]});
            var Q22;
            Q22=makeQuery(id+"F3.imprint","IMPRINT",FACE,{"disambiguationData":[TD([[makeQuery(id+"F3.imprint","IMPRINT",EDGE,{"derivedFrom":sQuery(id+"F3.wireOp",EDGE,"E187.3")}),-1.0]])]});
            var Q23;
            Q23=makeQuery(id+"F3.imprint","IMPRINT",FACE,{"disambiguationData":[TD([[makeQuery(id+"F3.imprint","IMPRINT",EDGE,{"derivedFrom":sQuery(id+"F3.wireOp",EDGE,"E187.4")}),-1.0]])]});
            extrude(context, id + "F4", {"entities" : qUnion([Q0, Q1, Q2, Q3, Q4, Q5, Q6, Q7, Q8, Q9, Q10, Q11, Q12, Q13, Q14, Q15, Q16, Q17, Q18, Q19, Q20, Q21, Q22, Q23]), "operationType" : NewBodyOperationType.REMOVE, "oppositeDirection" : true, "depth" : 1.5 * mm});
        }
        {
            var Q0;
            Q0=makeQuery(id+"F3.imprint","IMPRINT",FACE,{"disambiguationData":[TD([[makeQuery(id+"F3.imprint","IMPRINT",EDGE,{"derivedFrom":sQuery(id+"F3.wireOp",EDGE,"E140.1")}),-1.0]])]});
            var Q1;
            Q1=makeQuery(id+"F3.imprint","IMPRINT",FACE,{"disambiguationData":[TD([[makeQuery(id+"F3.imprint","IMPRINT",EDGE,{"derivedFrom":sQuery(id+"F3.wireOp",EDGE,"E139.36")}),-1.0]])]});
            var Q2;
            Q2=makeQuery(id+"F3.imprint","IMPRINT",FACE,{"disambiguationData":[TD([[makeQuery(id+"F3.imprint","IMPRINT",EDGE,{"derivedFrom":sQuery(id+"F3.wireOp",EDGE,"E139.37")}),-1.0]])]});
            var Q3;
            Q3=makeQuery(id+"F3.imprint","IMPRINT",FACE,{"disambiguationData":[TD([[makeQuery(id+"F3.imprint","IMPRINT",EDGE,{"derivedFrom":sQuery(id+"F3.wireOp",EDGE,"E139.38")}),-1.0]])]});
            var Q4;
            Q4=makeQuery(id+"F3.imprint","IMPRINT",FACE,{"disambiguationData":[TD([[makeQuery(id+"F3.imprint","IMPRINT",EDGE,{"derivedFrom":sQuery(id+"F3.wireOp",EDGE,"E139.39")}),-1.0]])]});
            var Q5;
            Q5=makeQuery(id+"F3.imprint","IMPRINT",FACE,{"disambiguationData":[TD([[makeQuery(id+"F3.imprint","IMPRINT",EDGE,{"derivedFrom":sQuery(id+"F3.wireOp",EDGE,"E139.40")}),-1.0]])]});
            var Q6;
            Q6=makeQuery(id+"F3.imprint","IMPRINT",FACE,{"disambiguationData":[TD([[makeQuery(id+"F3.imprint","IMPRINT",EDGE,{"derivedFrom":sQuery(id+"F3.wireOp",EDGE,"E139.41")}),-1.0]])]});
            var Q7;
            Q7=makeQuery(id+"F3.imprint","IMPRINT",FACE,{"disambiguationData":[TD([[makeQuery(id+"F3.imprint","IMPRINT",EDGE,{"derivedFrom":sQuery(id+"F3.wireOp",EDGE,"E139.42")}),-1.0]])]});
            var Q8;
            Q8=makeQuery(id+"F3.imprint","IMPRINT",FACE,{"disambiguationData":[TD([[makeQuery(id+"F3.imprint","IMPRINT",EDGE,{"derivedFrom":sQuery(id+"F3.wireOp",EDGE,"E139.43")}),-1.0]])]});
            var Q9;
            Q9=makeQuery(id+"F3.imprint","IMPRINT",FACE,{"disambiguationData":[TD([[makeQuery(id+"F3.imprint","IMPRINT",EDGE,{"derivedFrom":sQuery(id+"F3.wireOp",EDGE,"E139.44")}),-1.0]])]});
            var Q10;
            Q10=makeQuery(id+"F3.imprint","IMPRINT",FACE,{"disambiguationData":[TD([[makeQuery(id+"F3.imprint","IMPRINT",EDGE,{"derivedFrom":sQuery(id+"F3.wireOp",EDGE,"E139.45")}),-1.0]])]});
            var Q11;
            Q11=makeQuery(id+"F3.imprint","IMPRINT",FACE,{"disambiguationData":[TD([[makeQuery(id+"F3.imprint","IMPRINT",EDGE,{"derivedFrom":sQuery(id+"F3.wireOp",EDGE,"E139.46")}),1.0]])]});
            var Q12;
            Q12=makeQuery(id+"F3.imprint","IMPRINT",FACE,{"disambiguationData":[TD([[makeQuery(id+"F3.imprint","IMPRINT",EDGE,{"derivedFrom":sQuery(id+"F3.wireOp",EDGE,"E139.47")}),1.0]])]});
            var Q13;
            Q13=makeQuery(id+"F3.imprint","IMPRINT",FACE,{"disambiguationData":[TD([[makeQuery(id+"F3.imprint","IMPRINT",EDGE,{"derivedFrom":sQuery(id+"F3.wireOp",EDGE,"E139.48")}),1.0]])]});
            var Q14;
            Q14=makeQuery(id+"F3.imprint","IMPRINT",FACE,{"disambiguationData":[TD([[makeQuery(id+"F3.imprint","IMPRINT",EDGE,{"derivedFrom":sQuery(id+"F3.wireOp",EDGE,"E139.30")}),1.0]])]});
            var Q15;
            Q15=makeQuery(id+"F3.imprint","IMPRINT",FACE,{"disambiguationData":[TD([[makeQuery(id+"F3.imprint","IMPRINT",EDGE,{"derivedFrom":sQuery(id+"F3.wireOp",EDGE,"E139.27")}),1.0]])]});
            var Q16;
            Q16=makeQuery(id+"F3.imprint","IMPRINT",FACE,{"disambiguationData":[TD([[makeQuery(id+"F3.imprint","IMPRINT",EDGE,{"derivedFrom":sQuery(id+"F3.wireOp",EDGE,"E140.2")}),-1.0]])]});
            var Q17;
            Q17=makeQuery(id+"F3.imprint","IMPRINT",FACE,{"disambiguationData":[TD([[makeQuery(id+"F3.imprint","IMPRINT",EDGE,{"derivedFrom":sQuery(id+"F3.wireOp",EDGE,"E140.3")}),-1.0]])]});
            var Q18;
            Q18=makeQuery(id+"F3.imprint","IMPRINT",FACE,{"disambiguationData":[TD([[makeQuery(id+"F3.imprint","IMPRINT",EDGE,{"derivedFrom":sQuery(id+"F3.wireOp",EDGE,"E139.29")}),1.0]])]});
            var Q19;
            Q19=makeQuery(id+"F3.imprint","IMPRINT",FACE,{"disambiguationData":[TD([[makeQuery(id+"F3.imprint","IMPRINT",EDGE,{"derivedFrom":sQuery(id+"F3.wireOp",EDGE,"E139.31")}),1.0]])]});
            var Q20;
            Q20=makeQuery(id+"F3.imprint","IMPRINT",FACE,{"disambiguationData":[TD([[makeQuery(id+"F3.imprint","IMPRINT",EDGE,{"derivedFrom":sQuery(id+"F3.wireOp",EDGE,"E139.32")}),1.0]])]});
            var Q21;
            Q21=makeQuery(id+"F3.imprint","IMPRINT",FACE,{"disambiguationData":[TD([[makeQuery(id+"F3.imprint","IMPRINT",EDGE,{"derivedFrom":sQuery(id+"F3.wireOp",EDGE,"E139.34")}),1.0]])]});
            var Q22;
            Q22=makeQuery(id+"F3.imprint","IMPRINT",FACE,{"disambiguationData":[TD([[makeQuery(id+"F3.imprint","IMPRINT",EDGE,{"derivedFrom":sQuery(id+"F3.wireOp",EDGE,"E139.33")}),1.0]])]});
            var Q23;
            Q23=makeQuery(id+"F3.imprint","IMPRINT",FACE,{"disambiguationData":[TD([[makeQuery(id+"F3.imprint","IMPRINT",EDGE,{"derivedFrom":sQuery(id+"F3.wireOp",EDGE,"E139.35")}),-1.0]])]});
            var Q24;
            Q24=makeQuery(id+"F3.imprint","IMPRINT",FACE,{"disambiguationData":[TD([[makeQuery(id+"F3.imprint","IMPRINT",EDGE,{"derivedFrom":sQuery(id+"F3.wireOp",EDGE,"E140.0")}),-1.0]])]});
            var Q25;
            Q25=makeQuery(id+"F3.imprint","IMPRINT",FACE,{"disambiguationData":[TD([[makeQuery(id+"F3.imprint","IMPRINT",EDGE,{"derivedFrom":sQuery(id+"F3.wireOp",EDGE,"E139.28")}),1.0]])]});
            var Q26;
            Q26=makeQuery(id+"F3.imprint","IMPRINT",FACE,{"disambiguationData":[TD([[makeQuery(id+"F3.imprint","IMPRINT",EDGE,{"derivedFrom":sQuery(id+"F3.wireOp",EDGE,"E187.0")}),-1.0]])]});
            extrude(context, id + "F5", {"entities" : qUnion([Q0, Q1, Q2, Q3, Q4, Q5, Q6, Q7, Q8, Q9, Q10, Q11, Q12, Q13, Q14, Q15, Q16, Q17, Q18, Q19, Q20, Q21, Q22, Q23, Q24, Q25, Q26]), "operationType" : NewBodyOperationType.REMOVE, "oppositeDirection" : true, "depth" : 2 * mm});
        }
        {
            var Q0;
            Q0=qCreatedBy(makeId("Top.planeOp"),FACE);
            var sketch = newSketch(context, id + "F6", { "sketchPlane" : qUnion([Q0])});
            skCircle(sketch, "E193", {"center": v(-351.88, 146.77) * mm, "radius": 2.6 * mm});
            skCircle(sketch, "E194", {"center": v(-351.88, 146.77) * mm, "radius": 4 * mm});
            skCircle(sketch, "E195", {"center": v(-351.88, 129.43) * mm, "radius": 3 * mm});
            skCircle(sketch, "E196", {"center": v(-351.88, 129.43) * mm, "radius": 1.6 * mm});
            skCircle(sketch, "E197", {"center": v(-328.87, 125.57) * mm, "radius": 4.06 * mm});
            skCircle(sketch, "E198", {"center": v(-328.87, 125.57) * mm, "radius": 6.44 * mm});
            skCircle(sketch, "E199", {"center": v(-328.87, 125.57) * mm, "radius": 9.26 * mm});
            skCircle(sketch, "E200", {"center": v(-325, 147.79) * mm, "radius": 4.8 * mm});
            skSolve(sketch);
        }
        {
            var Q0;
            Q0=makeQuery(id+"F6.imprint","IMPRINT",FACE,{"disambiguationData":[TD([[makeQuery(id+"F6.imprint","IMPRINT",EDGE,{"derivedFrom":sQuery(id+"F6.wireOp",EDGE,"E195")}),1.0]])]});
            var Q1;
            Q1=makeQuery(id+"F6.imprint","IMPRINT",FACE,{"disambiguationData":[TD([[makeQuery(id+"F6.imprint","IMPRINT",EDGE,{"derivedFrom":sQuery(id+"F6.wireOp",EDGE,"E193")}),-1.0]])]});
            extrude(context, id + "F7", {"entities" : qUnion([Q0, Q1]), "depth" : 5 * mm});
        }
        {
            var Q0;
            Q0=makeQuery(id+"F6.imprint","IMPRINT",FACE,{"disambiguationData":[TD([[makeQuery(id+"F6.imprint","IMPRINT",EDGE,{"derivedFrom":sQuery(id+"F6.wireOp",EDGE,"E193")}),-1.0]])]});
            var Q1;
            Q1=makeQuery(id+"F6.imprint","IMPRINT",FACE,{"disambiguationData":[TD([[makeQuery(id+"F6.imprint","IMPRINT",EDGE,{"derivedFrom":sQuery(id+"F6.wireOp",EDGE,"E195")}),1.0]])]});
            extrude(context, id + "F8", {"entities" : qUnion([Q0, Q1]), "depth" : 10 * mm});
        }
        {
            var Q0;
            Q0=makeQuery(id+"F0.imprint","IMPRINT",FACE,{"disambiguationData":[TD([[makeQuery(id+"F0.imprint","IMPRINT",EDGE,{"derivedFrom":sQuery(id+"F0.wireOp",EDGE,"E7")}),-1.0]])]});
            var sketch = newSketch(context, id + "F9", { "sketchPlane" : qUnion([Q0])});
            skLineSegment(sketch, "E201.0", {"start": v(-237.36, 309.29) * mm, "end": v(-237.36, -150.71) * mm});
            skLineSegment(sketch, "E201.1", {"start": v(-237.36, 309.29) * mm, "end": v(262.64, 309.29) * mm});
            skLineSegment(sketch, "E201.2", {"start": v(262.64, 309.29) * mm, "end": v(262.64, -150.71) * mm});
            skLineSegment(sketch, "E201.3", {"start": v(-237.36, -150.71) * mm, "end": v(262.64, -150.71) * mm});
            skCircle(sketch, "E201.4", {"center": v(-211.36, -124.71) * mm, "radius": 7.5 * mm});
            skCircle(sketch, "E201.5", {"center": v(236.64, -124.71) * mm, "radius": 7.5 * mm});
            skCircle(sketch, "E201.6", {"center": v(12.64, 283.29) * mm, "radius": 7.5 * mm});
            skCircle(sketch, "E201.7", {"center": v(116.64, 283.29) * mm, "radius": 7.5 * mm});
            skCircle(sketch, "E201.8", {"center": v(-91.36, 283.29) * mm, "radius": 7.5 * mm});
            skLineSegment(sketch, "E201.9", {"start": v(-118.36, 199.29) * mm, "end": v(182.64, 199.29) * mm});
            skLineSegment(sketch, "E201.10", {"start": v(182.64, 199.29) * mm, "end": v(182.64, -100.71) * mm});
            skLineSegment(sketch, "E201.12", {"start": v(-118.36, -100.71) * mm, "end": v(182.64, -100.71) * mm});
            skLineSegment(sketch, "E202.0", {"start": v(-117.36, 199.29) * mm, "end": v(-117.36, -100.71) * mm});
            skPoint(sketch, "E203.orphan", {"position": v(-117.36, -150.71) * mm});
            skPoint(sketch, "E204.orphan", {"position": v(182.64, -150.71) * mm});
            skPoint(sketch, "E205.orphan", {"position": v(182.64, 309.29) * mm});
            skPoint(sketch, "E206.orphan", {"position": v(-117.36, 309.29) * mm});
            skLineSegment(sketch, "E207.0", {"start": v(-558.04, -28.45) * mm, "end": v(-558.04, 1.55) * mm});
            skLineSegment(sketch, "E207.1", {"start": v(-558.04, 1.55) * mm, "end": v(-558.04, 53.55) * mm});
            skLineSegment(sketch, "E207.2", {"start": v(-473.04, 53.55) * mm, "end": v(-558.04, 53.55) * mm});
            skLineSegment(sketch, "E207.3", {"start": v(-473.04, -28.45) * mm, "end": v(-473.04, 53.55) * mm});
            skLineSegment(sketch, "E207.4", {"start": v(-473.04, -28.45) * mm, "end": v(-558.04, -28.45) * mm});
            skCircle(sketch, "E207.5", {"center": v(-494.04, -13.45) * mm, "radius": 8.5 * mm});
            skCircle(sketch, "E207.6", {"center": v(-537.04, -13.45) * mm, "radius": 8.5 * mm});
            skLineSegment(sketch, "E207.7", {"start": v(-473.04, 75.55) * mm, "end": v(-558.04, 75.55) * mm});
            skLineSegment(sketch, "E208.bottom", {"start": v(-568.04, 85.55) * mm, "end": v(-463.04, 85.55) * mm});
            skLineSegment(sketch, "E208.top", {"start": v(-568.04, -38.45) * mm, "end": v(-463.04, -38.45) * mm});
            skLineSegment(sketch, "E208.left", {"start": v(-568.04, 85.55) * mm, "end": v(-568.04, -38.45) * mm});
            skLineSegment(sketch, "E208.right", {"start": v(-463.04, 85.55) * mm, "end": v(-463.04, -38.45) * mm});
            skLineSegment(sketch, "E209.bottom", {"start": v(-127.36, 209.29) * mm, "end": v(192.64, 209.29) * mm});
            skLineSegment(sketch, "E209.top", {"start": v(-117.36, -110.71) * mm, "end": v(192.64, -110.71) * mm});
            skLineSegment(sketch, "E209.left", {"start": v(-127.36, 199.29) * mm, "end": v(-127.36, 102.57) * mm});
            skLineSegment(sketch, "E209.right", {"start": v(192.64, 199.29) * mm, "end": v(192.64, 137.6) * mm});
            skLineSegment(sketch, "E210", {"start": v(32.64, -110.71) * mm, "end": v(32.64, -100.71) * mm, "construction": true});
            skLineSegment(sketch, "E211", {"start": v(32.64, 209.29) * mm, "end": v(32.64, 199.29) * mm, "construction": true});
            skLineSegment(sketch, "E212.0", {"start": v(-117.36, 209.29) * mm, "end": v(-117.36, 199.29) * mm, "construction": true});
            skLineSegment(sketch, "E213.0", {"start": v(182.64, 209.29) * mm, "end": v(182.64, 199.29) * mm, "construction": true});
            skLineSegment(sketch, "E214.0", {"start": v(-117.36, -110.71) * mm, "end": v(-117.36, -100.71) * mm, "construction": true});
            skLineSegment(sketch, "E215.0", {"start": v(182.64, -110.71) * mm, "end": v(182.64, -100.71) * mm, "construction": true});
            skCircle(sketch, "E216", {"center": v(-117.36, 204.29) * mm, "radius": 1.25 * mm});
            skCircle(sketch, "E217", {"center": v(182.64, 204.29) * mm, "radius": 1.25 * mm});
            skCircle(sketch, "E218", {"center": v(182.64, -105.71) * mm, "radius": 1.25 * mm});
            skCircle(sketch, "E219", {"center": v(-117.36, -105.71) * mm, "radius": 1.25 * mm});
            skLineSegment(sketch, "E220.0", {"start": v(-237.36, -135.71) * mm, "end": v(-222.36, -135.71) * mm});
            skLineSegment(sketch, "E221.0", {"start": v(247.64, 294.29) * mm, "end": v(247.64, 209.29) * mm});
            skLineSegment(sketch, "E222.0", {"start": v(-222.36, 294.29) * mm, "end": v(-111, 294.29) * mm});
            skArc(sketch, "E223.0", {"start": v(-111, 294.29) * mm, "mid": v(-91.36, 260.79) * mm, "end": v(-71.74, 294.29) * mm});
            skArc(sketch, "E224.0", {"start": v(-7, 294.29) * mm, "mid": v(12.64, 260.79) * mm, "end": v(32.26, 294.29) * mm});
            skArc(sketch, "E225.0", {"start": v(97, 294.29) * mm, "mid": v(116.64, 260.79) * mm, "end": v(136.26, 294.29) * mm});
            skArc(sketch, "E226.0", {"start": v(-231, -135.71) * mm, "mid": v(-227.27, -140.62) * mm, "end": v(-222.36, -144.34) * mm});
            skArc(sketch, "E227.0", {"start": v(247.64, -144.34) * mm, "mid": v(252.55, -140.62) * mm, "end": v(256.26, -135.71) * mm});
            skLineSegment(sketch, "E228.trimOffspring", {"start": v(-222.36, -135.71) * mm, "end": v(-222.36, -150.71) * mm});
            skArc(sketch, "E229.trimOffspring", {"start": v(-191.74, -135.71) * mm, "mid": v(-195.45, -108.8) * mm, "end": v(-222.36, -105.09) * mm});
            skLineSegment(sketch, "E230.trimOffspring", {"start": v(-191.74, -135.71) * mm, "end": v(-141.5, -135.71) * mm});
            skLineSegment(sketch, "E231.trimOffspring", {"start": v(247.64, -135.71) * mm, "end": v(262.64, -135.71) * mm});
            skLineSegment(sketch, "E232.trimOffspring", {"start": v(247.64, -135.71) * mm, "end": v(247.64, -150.71) * mm});
            skArc(sketch, "E233.trimOffspring", {"start": v(247.64, -105.09) * mm, "mid": v(220.73, -108.8) * mm, "end": v(217, -135.71) * mm});
            skLineSegment(sketch, "E234.trimOffspring", {"start": v(136.26, 294.29) * mm, "end": v(247.64, 294.29) * mm});
            skLineSegment(sketch, "E235.trimOffspring", {"start": v(32.26, 294.29) * mm, "end": v(97, 294.29) * mm});
            skLineSegment(sketch, "E236.trimOffspring", {"start": v(-71.74, 294.29) * mm, "end": v(-7, 294.29) * mm});
            skLineSegment(sketch, "E237", {"start": v(192.64, 209.29) * mm, "end": v(247.64, 209.29) * mm});
            skLineSegment(sketch, "E238.0", {"start": v(206.03, 199.29) * mm, "end": v(247.64, 199.29) * mm});
            skLineSegment(sketch, "E239.0", {"start": v(-118.36, 189.29) * mm, "end": v(-117.36, 189.29) * mm});
            skLineSegment(sketch, "E240.0", {"start": v(172.64, 189.29) * mm, "end": v(172.64, -90.71) * mm});
            skLineSegment(sketch, "E241.0", {"start": v(-107.36, 189.29) * mm, "end": v(-107.36, -90.71) * mm});
            skLineSegment(sketch, "E242.0", {"start": v(-118.36, -90.71) * mm, "end": v(-117.36, -90.71) * mm});
            skLineSegment(sketch, "E243.trimOffspring", {"start": v(-107.36, -90.71) * mm, "end": v(172.64, -90.71) * mm});
            skLineSegment(sketch, "E244.trimOffspring", {"start": v(-107.36, 189.29) * mm, "end": v(172.64, 189.29) * mm});
            skLineSegment(sketch, "E245.0", {"start": v(-42.36, 189.29) * mm, "end": v(-42.36, -90.71) * mm});
            skLineSegment(sketch, "E246.0", {"start": v(-32.36, 189.29) * mm, "end": v(-32.36, -90.71) * mm});
            skLineSegment(sketch, "E247.0", {"start": v(27.64, 189.29) * mm, "end": v(27.64, -90.71) * mm});
            skLineSegment(sketch, "E248.0", {"start": v(37.64, 189.29) * mm, "end": v(37.64, -90.71) * mm});
            skLineSegment(sketch, "E249.0", {"start": v(97.64, 189.29) * mm, "end": v(97.64, -90.71) * mm});
            skLineSegment(sketch, "E250.0", {"start": v(107.64, 189.29) * mm, "end": v(107.64, -90.71) * mm});
            skLineSegment(sketch, "E251", {"start": v(-127.36, 209.29) * mm, "end": v(-222.36, 209.29) * mm});
            skLineSegment(sketch, "E252.0", {"start": v(-127.36, 199.29) * mm, "end": v(-222.36, 199.29) * mm});
            skLineSegment(sketch, "E253", {"start": v(-127.36, -110.71) * mm, "end": v(-127.36, -135.71) * mm});
            skLineSegment(sketch, "E254", {"start": v(192.64, -110.71) * mm, "end": v(192.64, -135.71) * mm});
            skLineSegment(sketch, "E255", {"start": v(192.64, -135.71) * mm, "end": v(247.64, -70.17) * mm});
            skLineSegment(sketch, "E256", {"start": v(-127.36, -135.71) * mm, "end": v(-222.36, -40.71) * mm});
            skLineSegment(sketch, "E257", {"start": v(192.64, -120.16) * mm, "end": v(247.64, -54.6) * mm});
            skLineSegment(sketch, "E258", {"start": v(247.64, -54.6) * mm, "end": v(192.64, -54.6) * mm});
            skLineSegment(sketch, "E259.0", {"start": v(247.64, -44.6) * mm, "end": v(192.64, -44.6) * mm});
            skLineSegment(sketch, "E260", {"start": v(247.64, -44.6) * mm, "end": v(192.64, 20.94) * mm});
            skLineSegment(sketch, "E261", {"start": v(247.64, -29.05) * mm, "end": v(192.64, 36.5) * mm});
            skLineSegment(sketch, "E262", {"start": v(192.64, 36.5) * mm, "end": v(247.64, 36.5) * mm});
            skLineSegment(sketch, "E263.0", {"start": v(192.64, 46.5) * mm, "end": v(247.64, 46.5) * mm});
            skLineSegment(sketch, "E264", {"start": v(192.64, 46.5) * mm, "end": v(247.64, 112.04) * mm});
            skLineSegment(sketch, "E265", {"start": v(192.64, 62.05) * mm, "end": v(247.64, 127.6) * mm});
            skLineSegment(sketch, "E266", {"start": v(247.64, 127.6) * mm, "end": v(192.64, 127.6) * mm});
            skLineSegment(sketch, "E267.0", {"start": v(247.64, 137.6) * mm, "end": v(192.64, 137.6) * mm});
            skLineSegment(sketch, "E268", {"start": v(247.64, 137.6) * mm, "end": v(192.64, 199.29) * mm});
            skLineSegment(sketch, "E269", {"start": v(206.03, 199.29) * mm, "end": v(247.64, 152.62) * mm});
            skLineSegment(sketch, "E270.trimOffspring", {"start": v(247.64, 112.04) * mm, "end": v(247.64, 46.5) * mm});
            skLineSegment(sketch, "E271.trimOffspring", {"start": v(247.64, 199.29) * mm, "end": v(247.64, 152.62) * mm});
            skLineSegment(sketch, "E272.trimOffspring", {"start": v(192.64, 127.6) * mm, "end": v(192.64, 62.05) * mm});
            skLineSegment(sketch, "E273.trimOffspring", {"start": v(192.64, 20.94) * mm, "end": v(192.64, -110.71) * mm});
            skLineSegment(sketch, "E274.trimOffspring", {"start": v(247.64, 36.5) * mm, "end": v(247.64, -29.05) * mm});
            skLineSegment(sketch, "E275.trimOffspring", {"start": v(247.64, -70.17) * mm, "end": v(247.64, -105.09) * mm});
            skLineSegment(sketch, "E276", {"start": v(-141.5, -135.71) * mm, "end": v(-222.36, -54.86) * mm});
            skLineSegment(sketch, "E277", {"start": v(-222.36, -40.71) * mm, "end": v(-127.36, -40.71) * mm});
            skLineSegment(sketch, "E278.0", {"start": v(-222.36, -30.71) * mm, "end": v(-127.36, -30.71) * mm});
            skLineSegment(sketch, "E279", {"start": v(-222.36, -30.71) * mm, "end": v(-127.36, 64.29) * mm});
            skLineSegment(sketch, "E280", {"start": v(-222.36, -16.57) * mm, "end": v(-127.36, 78.43) * mm});
            skLineSegment(sketch, "E281", {"start": v(-127.36, 78.43) * mm, "end": v(-222.36, 78.43) * mm});
            skLineSegment(sketch, "E282", {"start": v(-222.36, 88.43) * mm, "end": v(-127.36, 88.43) * mm});
            skLineSegment(sketch, "E283", {"start": v(-127.36, 88.43) * mm, "end": v(-222.36, 183.43) * mm});
            skLineSegment(sketch, "E284", {"start": v(-127.36, 102.57) * mm, "end": v(-222.36, 197.57) * mm});
            skLineSegment(sketch, "E285.trimOffspring", {"start": v(-127.36, -135.71) * mm, "end": v(217, -135.71) * mm});
            skLineSegment(sketch, "E286.trimOffspring", {"start": v(-127.36, -40.71) * mm, "end": v(-127.36, -110.71) * mm});
            skLineSegment(sketch, "E287.trimOffspring", {"start": v(-127.36, 64.29) * mm, "end": v(-127.36, -30.71) * mm});
            skLineSegment(sketch, "E288.trimOffspring", {"start": v(-222.36, -54.86) * mm, "end": v(-222.36, -105.09) * mm});
            skLineSegment(sketch, "E289.trimOffspring", {"start": v(-222.36, 78.43) * mm, "end": v(-222.36, -16.57) * mm});
            skLineSegment(sketch, "E290.trimOffspring", {"start": v(-222.36, 199.29) * mm, "end": v(-222.36, 197.57) * mm});
            skLineSegment(sketch, "E291", {"start": v(-222.36, 294.29) * mm, "end": v(-222.36, 209.29) * mm});
            skLineSegment(sketch, "E292.trimOffspring", {"start": v(-222.36, 183.43) * mm, "end": v(-222.36, 88.43) * mm});
            skLineSegment(sketch, "E293", {"start": v(-222.36, 209.29) * mm, "end": v(-137.36, 294.29) * mm});
            skLineSegment(sketch, "E294", {"start": v(-222.36, 223.43) * mm, "end": v(-151.5, 294.29) * mm});
            skLineSegment(sketch, "E295", {"start": v(-127.36, 209.29) * mm, "end": v(-127.36, 294.29) * mm});
            skLineSegment(sketch, "E296.0", {"start": v(-117.36, 209.29) * mm, "end": v(-117.36, 294.29) * mm});
            skLineSegment(sketch, "E297", {"start": v(-117.36, 294.29) * mm, "end": v(-32.36, 209.29) * mm});
            skLineSegment(sketch, "E298", {"start": v(-18.22, 209.29) * mm, "end": v(-75.89, 266.95) * mm});
            skLineSegment(sketch, "E299", {"start": v(-18.22, 209.29) * mm, "end": v(-18.22, 294.29) * mm});
            skLineSegment(sketch, "E300.0", {"start": v(-8.22, 209.29) * mm, "end": v(-8.22, 294.29) * mm});
            skLineSegment(sketch, "E301", {"start": v(-8.22, 209.29) * mm, "end": v(76.78, 294.29) * mm});
            skLineSegment(sketch, "E302", {"start": v(5.92, 209.29) * mm, "end": v(90.92, 294.29) * mm});
            skLineSegment(sketch, "E303", {"start": v(90.92, 294.29) * mm, "end": v(90.92, 209.29) * mm});
            skLineSegment(sketch, "E304.0", {"start": v(100.92, 294.29) * mm, "end": v(100.92, 209.29) * mm});
            skLineSegment(sketch, "E305", {"start": v(100.92, 294.29) * mm, "end": v(185.92, 209.29) * mm});
            skLineSegment(sketch, "E306", {"start": v(200.06, 209.29) * mm, "end": v(115.06, 294.29) * mm});
            skLineSegment(sketch, "E307", {"start": v(200.06, 209.29) * mm, "end": v(200.06, 294.29) * mm});
            skLineSegment(sketch, "E308.0", {"start": v(210.06, 209.29) * mm, "end": v(210.06, 294.29) * mm});
            skSolve(sketch);
        }
        {
            var Q0;
            {var subQ0=sQuery(id+"F9.wireOp",EDGE,"E241.0");Q0=makeQuery(id+"F9.imprint","IMPRINT",FACE,{"disambiguationData":[TD([[makeQuery(id+"F9.imprint","IMPRINT",EDGE,{"derivedFrom":subQ0}),1.0]])]});}
            var sketch = newSketch(context, id + "F10", { "sketchPlane" : qUnion([Q0])});
            skLineSegment(sketch, "E309.0", {"start": v(-237.36, 309.29) * mm, "end": v(262.64, 309.29) * mm});
            skLineSegment(sketch, "E309.1", {"start": v(-237.36, 309.29) * mm, "end": v(-237.36, -150.71) * mm});
            skLineSegment(sketch, "E309.2", {"start": v(-237.36, -150.71) * mm, "end": v(262.64, -150.71) * mm});
            skLineSegment(sketch, "E309.3", {"start": v(262.64, 309.29) * mm, "end": v(262.64, -150.71) * mm});
            skCircle(sketch, "E309.4", {"center": v(12.64, 283.29) * mm, "radius": 7.5 * mm});
            skCircle(sketch, "E309.5", {"center": v(236.64, -124.71) * mm, "radius": 7.5 * mm});
            skCircle(sketch, "E309.6", {"center": v(-211.36, -124.71) * mm, "radius": 7.5 * mm});
            skCircle(sketch, "E309.7", {"center": v(-117.36, 204.29) * mm, "radius": 1.25 * mm});
            skCircle(sketch, "E309.8", {"center": v(-117.36, -105.71) * mm, "radius": 1.25 * mm});
            skCircle(sketch, "E309.9", {"center": v(182.64, -105.71) * mm, "radius": 1.25 * mm});
            skCircle(sketch, "E309.10", {"center": v(182.64, 204.29) * mm, "radius": 1.25 * mm});
            skLineSegment(sketch, "E309.11", {"start": v(-127.36, 209.29) * mm, "end": v(192.64, 209.29) * mm});
            skLineSegment(sketch, "E309.12", {"start": v(-117.36, -110.71) * mm, "end": v(192.64, -110.71) * mm});
            skLineSegment(sketch, "E310", {"start": v(-117.36, -110.71) * mm, "end": v(-128.56, -110.71) * mm});
            skLineSegment(sketch, "E311", {"start": v(-128.56, -110.71) * mm, "end": v(-127.36, 209.29) * mm});
            skLineSegment(sketch, "E312", {"start": v(192.64, 209.29) * mm, "end": v(192.64, -110.71) * mm});
            skSolve(sketch);
        }
        {
            var Q0;
            Q0=makeQuery(id+"F10.imprint","IMPRINT",FACE,{"disambiguationData":[TD([[makeQuery(id+"F10.imprint","IMPRINT",EDGE,{"derivedFrom":sQuery(id+"F10.wireOp",EDGE,"E309.0")}),-1.0]])]});
            var Q1;
            Q1=makeQuery(id+"F10.imprint","IMPRINT",FACE,{"disambiguationData":[TD([[makeQuery(id+"F10.imprint","IMPRINT",EDGE,{"derivedFrom":sQuery(id+"F10.wireOp",EDGE,"E309.7")}),-1.0]])]});
            var Q2;
            {var subQ0=sQuery(id+"F9.wireOp",EDGE,"E241.0");Q2=makeQuery(id+"F10.imprint","IMPRINT",FACE,{"disambiguationData":[TD([[makeQuery(id+"F10.imprint","IMPRINT",EDGE,{"derivedFrom":makeQuery(id+"F9.imprint","IMPRINT",EDGE,{"derivedFrom":subQ0})}),1.0]])]});}
            extrude(context, id + "F11", {"entities" : qUnion([Q0, Q1, Q2]), "depth" : 5 * mm});
        }
        {
            var Q0;
            Q0=makeQuery(id+"F10.imprint","IMPRINT",FACE,{"disambiguationData":[TD([[makeQuery(id+"F10.imprint","IMPRINT",EDGE,{"derivedFrom":sQuery(id+"F10.wireOp",EDGE,"E309.7")}),-1.0]])]});
            var Q1;
            {var subQ0=sQuery(id+"F9.wireOp",EDGE,"E241.0");Q1=makeQuery(id+"F10.imprint","IMPRINT",FACE,{"disambiguationData":[TD([[makeQuery(id+"F10.imprint","IMPRINT",EDGE,{"derivedFrom":makeQuery(id+"F9.imprint","IMPRINT",EDGE,{"derivedFrom":subQ0})}),1.0]])]});}
            extrude(context, id + "F12", {"entities" : qUnion([Q0, Q1]), "depth" : 3 * mm});
        }
    });
